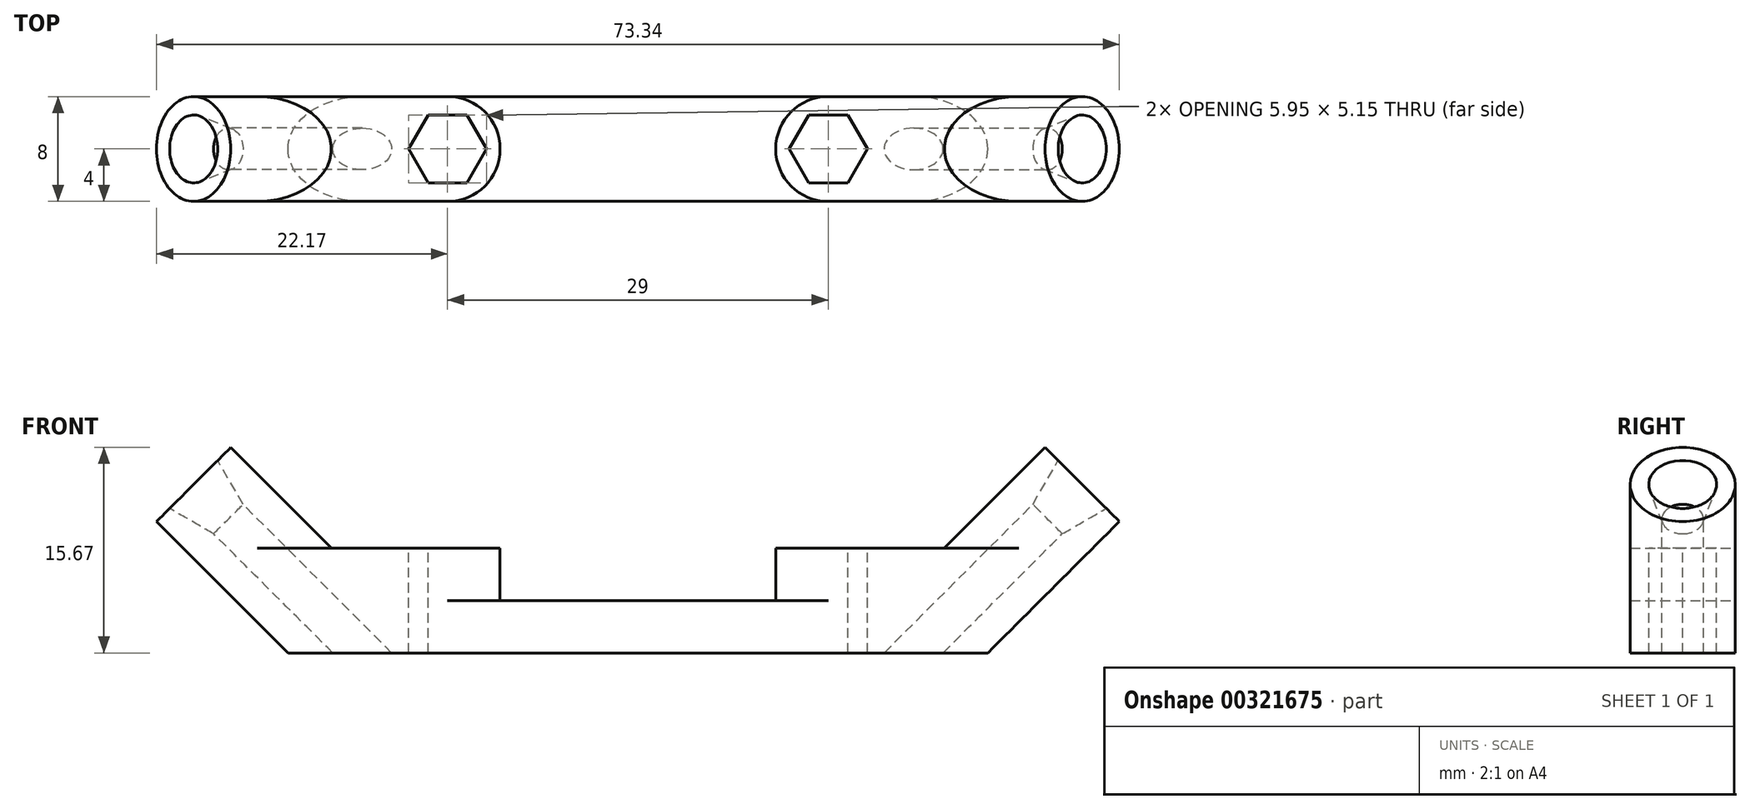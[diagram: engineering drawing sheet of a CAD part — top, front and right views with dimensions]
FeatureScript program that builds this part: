
annotation { "Feature Type Name" : "Feature", "Feature Type Description" : "" }
export const myFeature = defineFeature(function(context is Context, id is Id, definition is map)
    precondition{}
    {
        {
            var Q0;
            Q0=qCreatedBy(makeId("Front.planeOp"),FACE);
            var sketch = newSketch(context, id + "F0", { "sketchPlane" : qUnion([Q0])});
            skLineSegment(sketch, "E0", {"start": v(0, 0) * mm, "end": v(-26.66, 0) * mm});
            skLineSegment(sketch, "E1", {"start": v(-26.66, 0) * mm, "end": v(-34.66, 8) * mm});
            skLineSegment(sketch, "E2", {"start": v(-34.66, 8) * mm, "end": v(0, 8) * mm});
            skLineSegment(sketch, "E3", {"start": v(0, 8) * mm, "end": v(0, 0) * mm});
            skLineSegment(sketch, "E4", {"start": v(-29, 8) * mm, "end": v(-21, 0) * mm, "construction": true});
            skLineSegment(sketch, "E5", {"start": v(0, 8) * mm, "end": v(0, 31.76) * mm, "construction": true});
            skSolve(sketch);
        }
        {
            var Q0;
            Q0=qSketchRegion(id+"F0",true);
            extrude(context, id + "F1", {"entities" : qUnion([Q0]), "endBound" : BoundingType.SYMMETRIC, "depth" : 8 * mm});
        }
        {
            var Q0;
            Q0=makeQuery(id+"F1.opExtrude","CAP_EDGE",EDGE,{"disambiguationData":[OSD([sQuery(id+"F0.wireOp",EDGE,"E1")])],"isStart":true});
            var Q1;
            Q1=makeQuery(id+"F1.opExtrude","CAP_EDGE",EDGE,{"disambiguationData":[OSD([sQuery(id+"F0.wireOp",EDGE,"E1")])],"isStart":false});
            fillet(context, id + "F2", {"entities" : qUnion([Q0, Q1]), "radius" : 4 * mm, "tangentPropagation" : true, "allowEdgeOverflow" : false});
        }
        {
            var Q0;
            Q0=makeQuery(id+"F1.opExtrude","SWEPT_FACE",FACE,{"disambiguationData":[OSD([sQuery(id+"F0.wireOp",EDGE,"E2")])]});
            var sketch = newSketch(context, id + "F3", { "sketchPlane" : qUnion([Q0])});
            skLineSegment(sketch, "E6", {"start": v(-14.5, 0) * mm, "end": v(0, 0) * mm, "construction": true});
            skLineSegment(sketch, "E7", {"start": v(0, 0) * mm, "end": v(0, 20.84) * mm, "construction": true});
            skCircle(sketch, "E8.cCircle", {"center": v(-14.5, 0) * mm, "radius": 2.58 * mm, "construction": true});
            skLineSegment(sketch, "E8.0", {"start": v(-13.01, 2.57) * mm, "end": v(-11.53, 0) * mm});
            skLineSegment(sketch, "E8.1", {"start": v(-11.53, 0) * mm, "end": v(-13.01, -2.58) * mm});
            skLineSegment(sketch, "E8.2", {"start": v(-13.01, -2.58) * mm, "end": v(-15.99, -2.57) * mm});
            skLineSegment(sketch, "E8.3", {"start": v(-15.99, -2.57) * mm, "end": v(-17.47, 0) * mm});
            skLineSegment(sketch, "E8.4", {"start": v(-17.47, 0) * mm, "end": v(-15.99, 2.57) * mm});
            skLineSegment(sketch, "E8.5", {"start": v(-15.99, 2.58) * mm, "end": v(-13.01, 2.58) * mm});
            skPoint(sketch, "E8.0.midPoint", {"position": v(-12.27, 1.29) * mm});
            skSolve(sketch);
        }
        {
            var Q0;
            Q0=qSketchRegion(id+"F3",true);
            extrude(context, id + "F4", {"entities" : qUnion([Q0]), "operationType" : NewBodyOperationType.REMOVE, "endBound" : BoundingType.UP_TO_NEXT, "oppositeDirection" : true, "depth" : 25.4 * mm});
        }
        {
            var Q0;
            Q0=makeQuery(id+"F1.opExtrude","SWEPT_FACE",FACE,{"disambiguationData":[OSD([sQuery(id+"F0.wireOp",EDGE,"E2")])]});
            var sketch = newSketch(context, id + "F5", { "sketchPlane" : qUnion([Q0])});
            skArc(sketch, "E9", {"start": v(-14.5, -4) * mm, "mid": v(-10.5, 0) * mm, "end": v(-14.5, 4) * mm});
            skLineSegment(sketch, "E10", {"start": v(-14.5, 4) * mm, "end": v(0, 4) * mm});
            skLineSegment(sketch, "E11", {"start": v(0, 4) * mm, "end": v(0, -4) * mm});
            skLineSegment(sketch, "E12", {"start": v(0, -4) * mm, "end": v(-14.5, -4) * mm});
            skLineSegment(sketch, "E13", {"start": v(-14.5, -4) * mm, "end": v(-14.5, 4) * mm, "construction": true});
            skPoint(sketch, "E14", {"position": v(-14.5, 4) * mm});
            skPoint(sketch, "E15", {"position": v(-14.5, 2.58) * mm});
            skSolve(sketch);
        }
        {
            var Q0;
            Q0=qSketchRegion(id+"F5",true);
            extrude(context, id + "F6", {"entities" : qUnion([Q0]), "operationType" : NewBodyOperationType.REMOVE, "oppositeDirection" : true, "depth" : 4 * mm});
        }
        {
            var Q0;
            Q0=qCreatedBy(makeId("Front.planeOp"),FACE);
            var sketch = newSketch(context, id + "F7", { "sketchPlane" : qUnion([Q0])});
            skLineSegment(sketch, "E16", {"start": v(-10.3, -10.7) * mm, "end": v(-44.62, 23.62) * mm});
            skLineSegment(sketch, "E17", {"start": v(-44.62, 23.62) * mm, "end": v(-45.74, 22.5) * mm});
            skLineSegment(sketch, "E18", {"start": v(-45.74, 22.5) * mm, "end": v(-11.43, -11.81) * mm});
            skLineSegment(sketch, "E19", {"start": v(-11.43, -11.81) * mm, "end": v(-10.3, -10.7) * mm});
            skLineSegment(sketch, "E20", {"start": v(-38.6, 17.6) * mm, "end": v(-44.62, 23.62) * mm, "construction": true});
            skSolve(sketch);
        }
        {
            var Q0;
            Q0=sQuery(id+"F0.wireOp",EDGE,"E4");
            var Q1;
            Q1=sQuery(id+"F0.wireOp",VERTEX,"E4.start");
            cPlane(context, id + "F8", {"entities" : qUnion([Q0, Q1]), "cplaneType" : CPlaneType.LINE_POINT, "offset" : 25 * mm, "width" : 150 * mm, "height" : 150 * mm});
        }
        {
            var Q0;
            Q0=qCreatedBy(id+"F8.planeOp",FACE);
            var sketch = newSketch(context, id + "F9", { "sketchPlane" : qUnion([Q0])});
            skCircle(sketch, "E21", {"center": v(0, -14.85) * mm, "radius": 4 * mm});
            skSolve(sketch);
        }
        {
            var Q0;
            Q0=qSketchRegion(id+"F9",true);
            extrude(context, id + "F10", {"entities" : qUnion([Q0]), "operationType" : NewBodyOperationType.ADD, "endBound" : BoundingType.SYMMETRIC, "oppositeDirection" : true, "depth" : 13.7 * mm});
        }
        {
            var Q0;
            Q0=qSketchRegion(id+"F7",true);
            var Q1;
            Q1=sQuery(id+"F7.wireOp",EDGE,"E16");
            revolve(context, id + "F11", {"operationType" : NewBodyOperationType.REMOVE, "entities" : qUnion([Q0]), "axis" : qUnion([Q1]), "revolveType" : RevolveType.FULL, "oppositeDirection" : true});
        }
        {
            var Q0;
            Q0=makeQuery(id+"F11.boolean.opBoolean","INTERSECT",EDGE,{"derivedFrom":[makeQuery(id+"F10.opExtrude","CAP_FACE",FACE,{"disambiguationData":[OSD([sQuery(id+"F9.wireOp",EDGE,"E21")])],"isStart":false}),makeQuery(id+"F11.opRevolve","SWEPT_FACE",FACE,{"disambiguationData":[OSD([sQuery(id+"F7.wireOp",EDGE,"E18")])]})]});
            chamfer(context, id + "F12", {"entities" : qUnion([Q0]), "chamferType" : ChamferType.OFFSET_ANGLE, "width" : 1 * mm, "oppositeDirection" : false, "angle" : 75 * degree, "tangentPropagation" : true});
        }
        {
            var Q0;
            Q0=makeQuery(id+"F1.opExtrude","SWEPT_BODY",BODY,{"disambiguationData":[OSD([sQuery(id+"F0.wireOp",EDGE,"E0"),sQuery(id+"F0.wireOp",EDGE,"E1"),sQuery(id+"F0.wireOp",EDGE,"E2"),sQuery(id+"F0.wireOp",EDGE,"E3")])]});
            var Q1;
            Q1=makeQuery(id+"F1.opExtrude","SWEPT_FACE",FACE,{"disambiguationData":[OSD([sQuery(id+"F0.wireOp",EDGE,"E3")])]});
            mirror(context, id + "F13", {"operationType" : NewBodyOperationType.ADD, "entities" : qUnion([Q0]), "mirrorPlane" : qUnion([Q1])});
        }
    });
